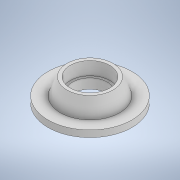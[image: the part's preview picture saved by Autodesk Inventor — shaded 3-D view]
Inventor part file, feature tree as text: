
AUTODESK INVENTOR PART (.ipt)
format: ipt  version: 2021 (Build 250183000, 183)  size: 123,904 bytes
history: native  units: mm
features: revolve x1, sketch x1
ambient origin geometry x8: Origin, YZ Plane, XZ Plane, XY Plane, X Axis, Y Axis, Z Axis, Center Point
bodies: Solid1 (feature_tree)
feature tree (2):
  revolve  "Revolution1"  [1 undecoded]
  sketch  "Sketch2"  dims[d0=11.99mm d1=1.5mm d2=2.0mm d3=15.0mm d4=6.0mm d5=8.0mm d6=0.0mm d7=4.0mm d8=7.5mm d9=90.0deg]
note: 1 required parameter value undecoded (feature->parameter linkage not recoverable at this tier; creation-order binding heuristic only, values carry confidence <= 0.55)
